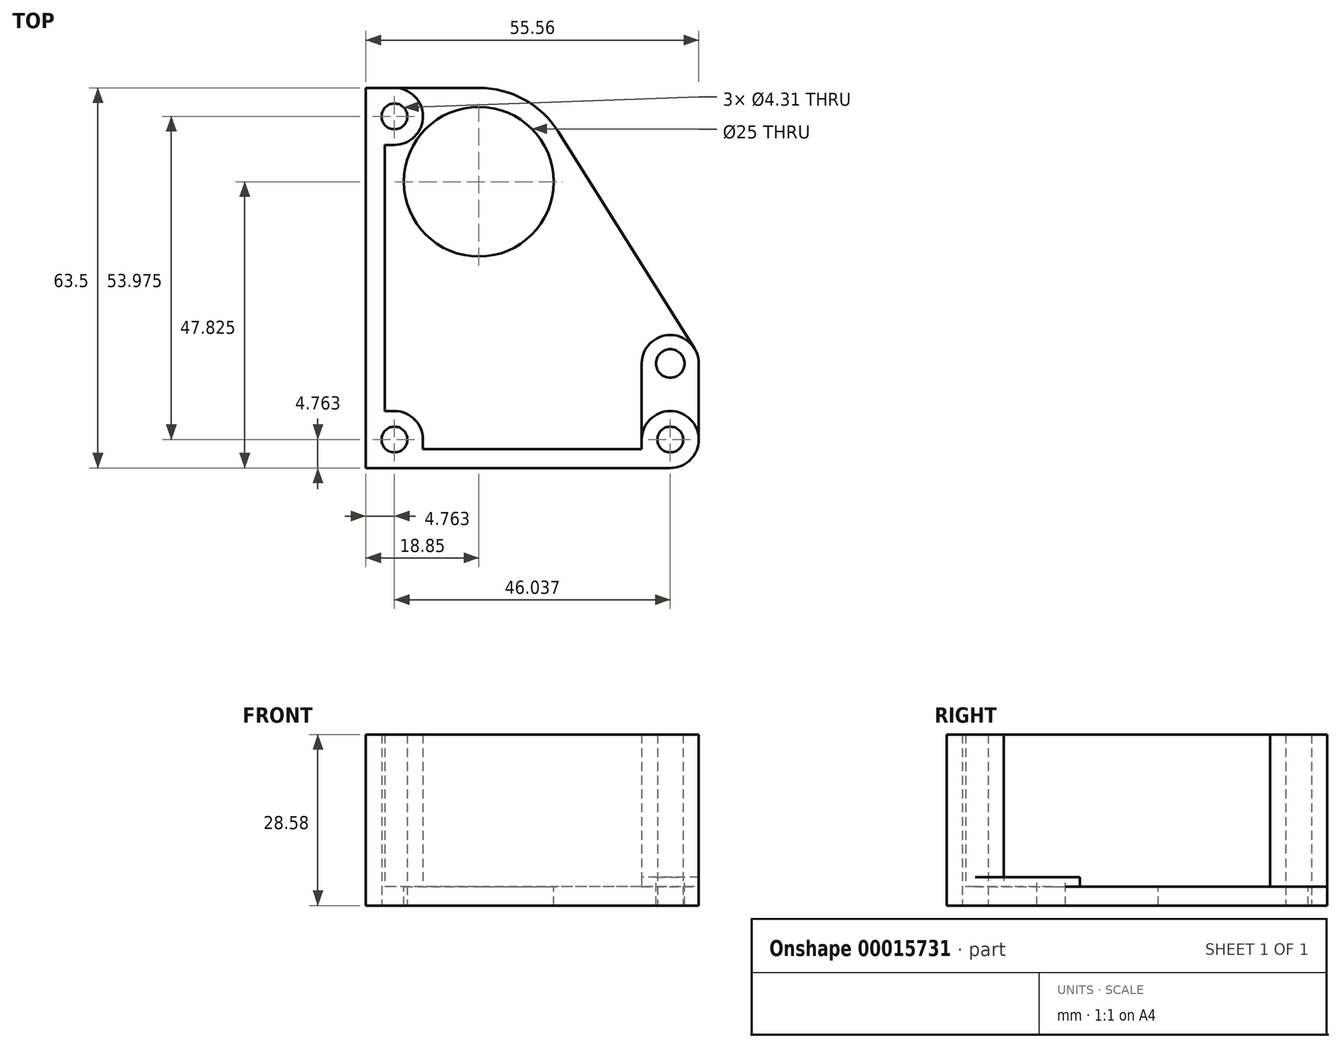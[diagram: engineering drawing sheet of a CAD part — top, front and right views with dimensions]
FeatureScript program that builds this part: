
annotation { "Feature Type Name" : "Feature", "Feature Type Description" : "" }
export const myFeature = defineFeature(function(context is Context, id is Id, definition is map)
    precondition{}
    {
        {
            var Q0;
            Q0=qCreatedBy(makeId("Top.planeOp"),FACE);
            var sketch = newSketch(context, id + "F0", { "sketchPlane" : qUnion([Q0])});
            skLineSegment(sketch, "E0.bottom", {"start": v(0, 0) * mm, "end": v(50.8, 0) * mm});
            skLineSegment(sketch, "E0.left", {"start": v(0, 0) * mm, "end": v(0, 63.5) * mm});
            skLineSegment(sketch, "E1", {"start": v(4.76, 0) * mm, "end": v(4.76, 4.76) * mm, "construction": true});
            skLineSegment(sketch, "E2", {"start": v(4.76, 4.76) * mm, "end": v(0, 4.76) * mm, "construction": true});
            skCircle(sketch, "E3", {"center": v(4.76, 4.76) * mm, "radius": 2.15 * mm});
            skCircle(sketch, "E4", {"center": v(50.8, 4.76) * mm, "radius": 2.15 * mm});
            skArc(sketch, "E5", {"start": v(50.8, 0) * mm, "mid": v(54.17, 8.13) * mm, "end": v(46.04, 4.76) * mm});
            skLineSegment(sketch, "E6", {"start": v(46.04, 4.76) * mm, "end": v(46.04, 3.18) * mm});
            skLineSegment(sketch, "E7", {"start": v(46.04, 3.18) * mm, "end": v(9.53, 3.17) * mm});
            skLineSegment(sketch, "E8", {"start": v(9.53, 4.76) * mm, "end": v(9.53, 3.17) * mm});
            skArc(sketch, "E9", {"start": v(9.53, 4.76) * mm, "mid": v(8.13, 8.13) * mm, "end": v(4.76, 9.52) * mm});
            skLineSegment(sketch, "E10", {"start": v(46.04, 3.18) * mm, "end": v(46.04, 0) * mm, "construction": true});
            skLineSegment(sketch, "E11", {"start": v(4.76, 9.52) * mm, "end": v(3.18, 9.52) * mm});
            skLineSegment(sketch, "E12", {"start": v(3.18, 9.52) * mm, "end": v(3.18, 53.98) * mm});
            skLineSegment(sketch, "E13", {"start": v(0, 63.5) * mm, "end": v(4.76, 63.5) * mm});
            skArc(sketch, "E14", {"start": v(4.76, 53.97) * mm, "mid": v(9.52, 58.74) * mm, "end": v(4.76, 63.5) * mm});
            skLineSegment(sketch, "E15", {"start": v(3.17, 53.98) * mm, "end": v(4.76, 53.98) * mm});
            skCircle(sketch, "E16", {"center": v(4.76, 58.74) * mm, "radius": 2.15 * mm});
            skLineSegment(sketch, "E17", {"start": v(50.8, 4.76) * mm, "end": v(50.8, 22.23) * mm, "construction": true});
            skLineSegment(sketch, "E18", {"start": v(4.76, 58.74) * mm, "end": v(23.08, 58.74) * mm, "construction": true});
            skLineSegment(sketch, "E19", {"start": v(23.08, 58.74) * mm, "end": v(23.08, 49.95) * mm, "construction": true});
            skLineSegment(sketch, "E20", {"start": v(23.08, 49.95) * mm, "end": v(50.8, 22.23) * mm, "construction": true});
            skSolve(sketch);
        }
        {
            var Q0;
            Q0=qSketchRegion(id+"F0",true);
            extrude(context, id + "F1", {"entities" : qUnion([Q0]), "depth" : 25.4 * mm});
        }
        {
            var Q0;
            Q0=makeQuery(id+"F1.opExtrude","CAP_FACE",FACE,{"disambiguationData":[OSD([sQuery(id+"F0.wireOp",EDGE,"E0.bottom"),sQuery(id+"F0.wireOp",EDGE,"E0.left"),sQuery(id+"F0.wireOp",EDGE,"E3"),sQuery(id+"F0.wireOp",EDGE,"E4"),sQuery(id+"F0.wireOp",EDGE,"E5"),sQuery(id+"F0.wireOp",EDGE,"E6"),sQuery(id+"F0.wireOp",EDGE,"E7"),sQuery(id+"F0.wireOp",EDGE,"E8"),sQuery(id+"F0.wireOp",EDGE,"E9"),sQuery(id+"F0.wireOp",EDGE,"E11"),sQuery(id+"F0.wireOp",EDGE,"E12"),sQuery(id+"F0.wireOp",EDGE,"E13"),sQuery(id+"F0.wireOp",EDGE,"E14"),sQuery(id+"F0.wireOp",EDGE,"E15"),sQuery(id+"F0.wireOp",EDGE,"E16")])],"isStart":true});
            var sketch = newSketch(context, id + "F2", { "sketchPlane" : qUnion([Q0])});
            skLineSegment(sketch, "E21", {"start": v(55.56, -17.46) * mm, "end": v(55.56, -4.76) * mm});
            skLineSegment(sketch, "E22.bottom", {"start": v(50.8, 0) * mm, "end": v(0, 0) * mm});
            skLineSegment(sketch, "E22.top", {"start": v(18.85, -63.5) * mm, "end": v(0, -63.5) * mm});
            skLineSegment(sketch, "E22.right", {"start": v(0, -63.5) * mm, "end": v(0, 0) * mm});
            skCircle(sketch, "E23", {"center": v(18.85, -47.82) * mm, "radius": 12.5 * mm});
            skLineSegment(sketch, "E24", {"start": v(18.85, -47.82) * mm, "end": v(6.35, -47.82) * mm, "construction": true});
            skLineSegment(sketch, "E25", {"start": v(6.35, -47.82) * mm, "end": v(3.18, -47.82) * mm, "construction": true});
            skLineSegment(sketch, "E26", {"start": v(50.8, -17.46) * mm, "end": v(50.8, -4.76) * mm, "construction": true});
            skCircle(sketch, "E27", {"center": v(4.76, -58.74) * mm, "radius": 2.15 * mm});
            skCircle(sketch, "E28", {"center": v(50.8, -4.76) * mm, "radius": 2.15 * mm});
            skCircle(sketch, "E29", {"center": v(4.76, -4.76) * mm, "radius": 2.15 * mm});
            skCircle(sketch, "E30", {"center": v(50.8, -17.46) * mm, "radius": 2.38 * mm});
            skArc(sketch, "E31", {"start": v(18.85, -63.5) * mm, "mid": v(26.43, -61.54) * mm, "end": v(32.13, -56.16) * mm});
            skArc(sketch, "E32", {"start": v(54.83, -20) * mm, "mid": v(55.38, -18.78) * mm, "end": v(55.56, -17.46) * mm});
            skLineSegment(sketch, "E33", {"start": v(54.83, -20) * mm, "end": v(32.13, -56.16) * mm});
            skSolve(sketch);
        }
        {
            var Q0;
            {var subQ1=sQuery(id+"F2.wireOp",EDGE,"E21");Q0=makeQuery(id+"F2.imprint","IMPRINT",FACE,{"disambiguationData":[TD([[makeQuery(id+"F2.imprint","IMPRINT",EDGE,{"derivedFrom":subQ1}),1.0]])]});}
            var Q1;
            {var subQ0=sQuery(id+"F2.wireOp",EDGE,"E22.bottom");Q1=makeQuery(id+"F2.imprint","IMPRINT",FACE,{"disambiguationData":[TD([[makeQuery(id+"F2.imprint","IMPRINT",EDGE,{"derivedFrom":subQ0}),1.0]])]});}
            var Q2;
            {var subQ3=sQuery(id+"F2.wireOp",EDGE,"E22.bottom");Q2=makeQuery(id+"F2.imprint","IMPRINT",FACE,{"disambiguationData":[TD([[makeQuery(id+"F2.imprint","IMPRINT",EDGE,{"derivedFrom":subQ3}),-1.0]])]});}
            extrude(context, id + "F3", {"entities" : qUnion([Q0, Q1, Q2]), "operationType" : NewBodyOperationType.ADD, "depth" : 3.17 * mm});
        }
        {
            var Q0;
            Q0=makeQuery(id+"F3.opExtrude","CAP_FACE",FACE,{"disambiguationData":[OSD([sQuery(id+"F0.wireOp",EDGE,"E5"),sQuery(id+"F2.wireOp",EDGE,"E21"),sQuery(id+"F2.wireOp",EDGE,"E22.bottom"),sQuery(id+"F2.wireOp",EDGE,"E22.top"),sQuery(id+"F2.wireOp",EDGE,"E22.right"),sQuery(id+"F2.wireOp",EDGE,"Oq1qHOtY-dPQz-0eYC-4kqj-wJRqUI8CF7o4"),sQuery(id+"F2.wireOp",EDGE,"cl1vHnk4-duGk-15BS-S358-VBLFIcnkvt8H"),sQuery(id+"F2.wireOp",EDGE,"E23"),sQuery(id+"F2.wireOp",EDGE,"eMZwRTUm-ZFuV-JSAQ-PJtg-uAEFUKO2sok6"),sQuery(id+"F2.wireOp",EDGE,"E27"),sQuery(id+"F2.wireOp",EDGE,"E28"),sQuery(id+"F2.wireOp",EDGE,"E29"),sQuery(id+"F2.wireOp",EDGE,"E30")])],"isStart":true});
            var sketch = newSketch(context, id + "F4", { "sketchPlane" : qUnion([Q0])});
            skLineSegment(sketch, "E34", {"start": v(55.56, 4.76) * mm, "end": v(55.56, 17.46) * mm});
            skLineSegment(sketch, "E35", {"start": v(46.04, 4.76) * mm, "end": v(46.04, 17.46) * mm});
            skCircle(sketch, "E36", {"center": v(50.8, 17.46) * mm, "radius": 2.38 * mm});
            skArc(sketch, "E37", {"start": v(55.56, 17.46) * mm, "mid": v(50.8, 22.22) * mm, "end": v(46.04, 17.46) * mm});
            skArc(sketch, "E38", {"start": v(55.56, 4.76) * mm, "mid": v(50.8, 9.53) * mm, "end": v(46.04, 4.76) * mm});
            skSolve(sketch);
        }
        {
            var Q0;
            Q0=qSketchRegion(id+"F4",true);
            extrude(context, id + "F5", {"entities" : qUnion([Q0]), "operationType" : NewBodyOperationType.ADD, "depth" : 1.59 * mm});
        }
    });
